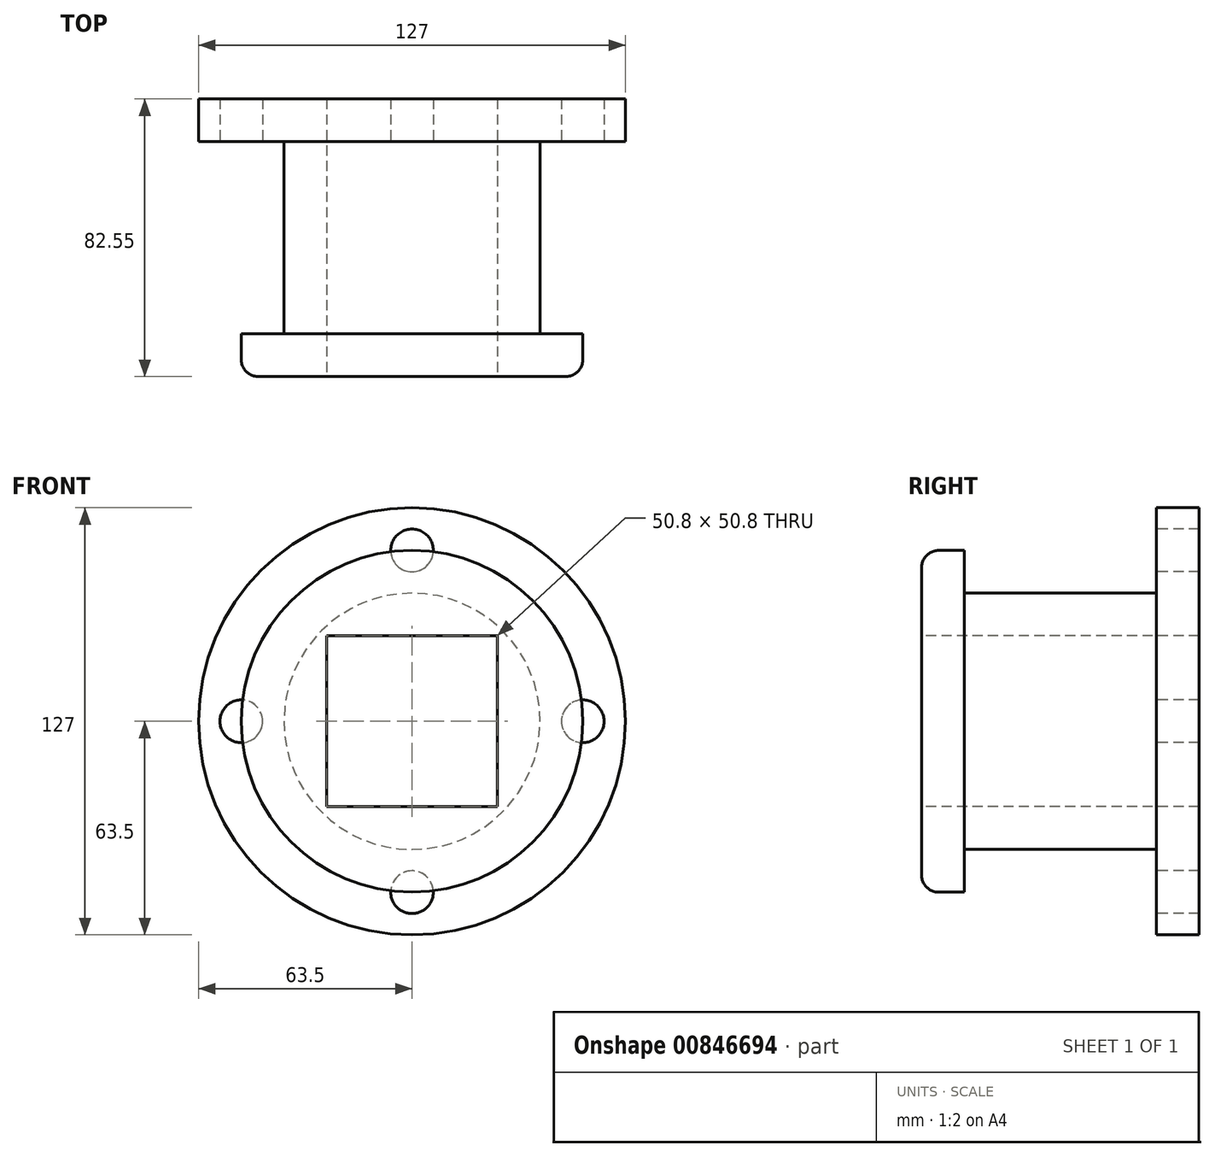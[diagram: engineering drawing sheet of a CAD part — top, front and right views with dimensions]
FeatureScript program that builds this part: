
annotation { "Feature Type Name" : "Feature", "Feature Type Description" : "" }
export const myFeature = defineFeature(function(context is Context, id is Id, definition is map)
    precondition{}
    {
        {
            var Q0;
            Q0=qCreatedBy(makeId("Front.planeOp"),FACE);
            var sketch = newSketch(context, id + "F0", { "sketchPlane" : qUnion([Q0])});
            skCircle(sketch, "E0", {"center": v(0, 0) * mm, "radius": 63.5 * mm});
            skSolve(sketch);
        }
        {
            var Q0;
            Q0 = qSketchRegion(id + "F0", true);
            extrude(context, id + "F1", {"entities" : qUnion([Q0]), "depth" : 12.7 * mm, "offsetDistance" : 25.4 * mm});
        }
        {
            var Q0;
            Q0=makeQuery(id+"F0.imprint","IMPRINT",FACE,{"disambiguationData":[TD([[makeQuery(id+"F0.imprint","IMPRINT",EDGE,{"derivedFrom":sQuery(id+"F0.wireOp",EDGE,"E0")}),1.0]])]});
            extrude(context, id + "F2", {"entities" : qUnion([Q0]), "operationType" : NewBodyOperationType.ADD, "depth" : 12.7 * mm, "offsetDistance" : 25.4 * mm});
        }
        {
            var Q0;
            Q0=makeQuery(id+"F1.opExtrude","CAP_FACE",FACE,{"disambiguationData":[OSD([sQuery(id+"F0.wireOp",EDGE,"E0")])],"isStart":false});
            var sketch = newSketch(context, id + "F3", { "sketchPlane" : qUnion([Q0])});
            skCircle(sketch, "E1", {"center": v(-50.8, 0) * mm, "radius": 6.35 * mm});
            skCircle(sketch, "E2", {"center": v(0, 50.8) * mm, "radius": 6.35 * mm});
            skCircle(sketch, "E3", {"center": v(50.8, 0) * mm, "radius": 6.35 * mm});
            skCircle(sketch, "E4", {"center": v(0, -50.8) * mm, "radius": 6.35 * mm});
            skPoint(sketch, "E5.orphan", {"position": v(0, 0) * mm});
            skSolve(sketch);
        }
        {
            var Q0;
            Q0 = qSketchRegion(id + "F3", true);
            extrude(context, id + "F4", {"entities" : qUnion([Q0]), "operationType" : NewBodyOperationType.REMOVE, "oppositeDirection" : true, "depth" : 25.4 * mm, "offsetDistance" : 25.4 * mm});
        }
        {
            var Q0;
            Q0=makeQuery(id+"F1.opExtrude","CAP_FACE",FACE,{"disambiguationData":[OSD([sQuery(id+"F0.wireOp",EDGE,"E0")])],"isStart":false});
            var sketch = newSketch(context, id + "F5", { "sketchPlane" : qUnion([Q0])});
            skCircle(sketch, "E6", {"center": v(0, 0) * mm, "radius": 38.1 * mm});
            skSolve(sketch);
        }
        {
            var Q0;
            Q0 = qSketchRegion(id + "F5", true);
            extrude(context, id + "F6", {"entities" : qUnion([Q0]), "operationType" : NewBodyOperationType.ADD, "depth" : 57.15 * mm, "offsetDistance" : 25.4 * mm});
        }
        {
            var Q0;
            Q0=makeQuery(id+"F6.opExtrude","CAP_FACE",FACE,{"disambiguationData":[OSD([sQuery(id+"F5.wireOp",EDGE,"E6")])],"isStart":false});
            var sketch = newSketch(context, id + "F7", { "sketchPlane" : qUnion([Q0])});
            skCircle(sketch, "E7", {"center": v(0, 0) * mm, "radius": 50.8 * mm});
            skSolve(sketch);
        }
        {
            var Q0;
            Q0 = qSketchRegion(id + "F7", true);
            extrude(context, id + "F8", {"entities" : qUnion([Q0]), "operationType" : NewBodyOperationType.ADD, "depth" : 12.7 * mm, "offsetDistance" : 25.4 * mm});
        }
        {
            var Q0;
            Q0=makeQuery(id+"F8.opExtrude","CAP_FACE",FACE,{"disambiguationData":[OSD([sQuery(id+"F7.wireOp",EDGE,"E7")])],"isStart":false});
            var sketch = newSketch(context, id + "F9", { "sketchPlane" : qUnion([Q0])});
            skLineSegment(sketch, "E8.bottom", {"start": v(25.4, 25.4) * mm, "end": v(-25.4, 25.4) * mm});
            skLineSegment(sketch, "E8.top", {"start": v(25.4, -25.4) * mm, "end": v(-25.4, -25.4) * mm});
            skLineSegment(sketch, "E8.left", {"start": v(25.4, 25.4) * mm, "end": v(25.4, -25.4) * mm});
            skLineSegment(sketch, "E8.right", {"start": v(-25.4, 25.4) * mm, "end": v(-25.4, -25.4) * mm});
            skPoint(sketch, "E8.middle", {"position": v(0, 0) * mm});
            skSolve(sketch);
        }
        {
            var Q0;
            Q0 = qSketchRegion(id + "F9", true);
            extrude(context, id + "F10", {"entities" : qUnion([Q0]), "operationType" : NewBodyOperationType.REMOVE, "oppositeDirection" : true, "depth" : 101.6 * mm, "offsetDistance" : 25.4 * mm});
        }
        {
            var Q0;
            Q0=makeQuery(id+"F8.opExtrude","CAP_EDGE",EDGE,{"disambiguationData":[OSD([sQuery(id+"F7.wireOp",EDGE,"E7")])],"isStart":false});
            fillet(context, id + "F11", {"entities" : qUnion([Q0]), "radius" : 5.08 * mm, "tangentPropagation" : true, "allowEdgeOverflow" : false});
        }
    });
